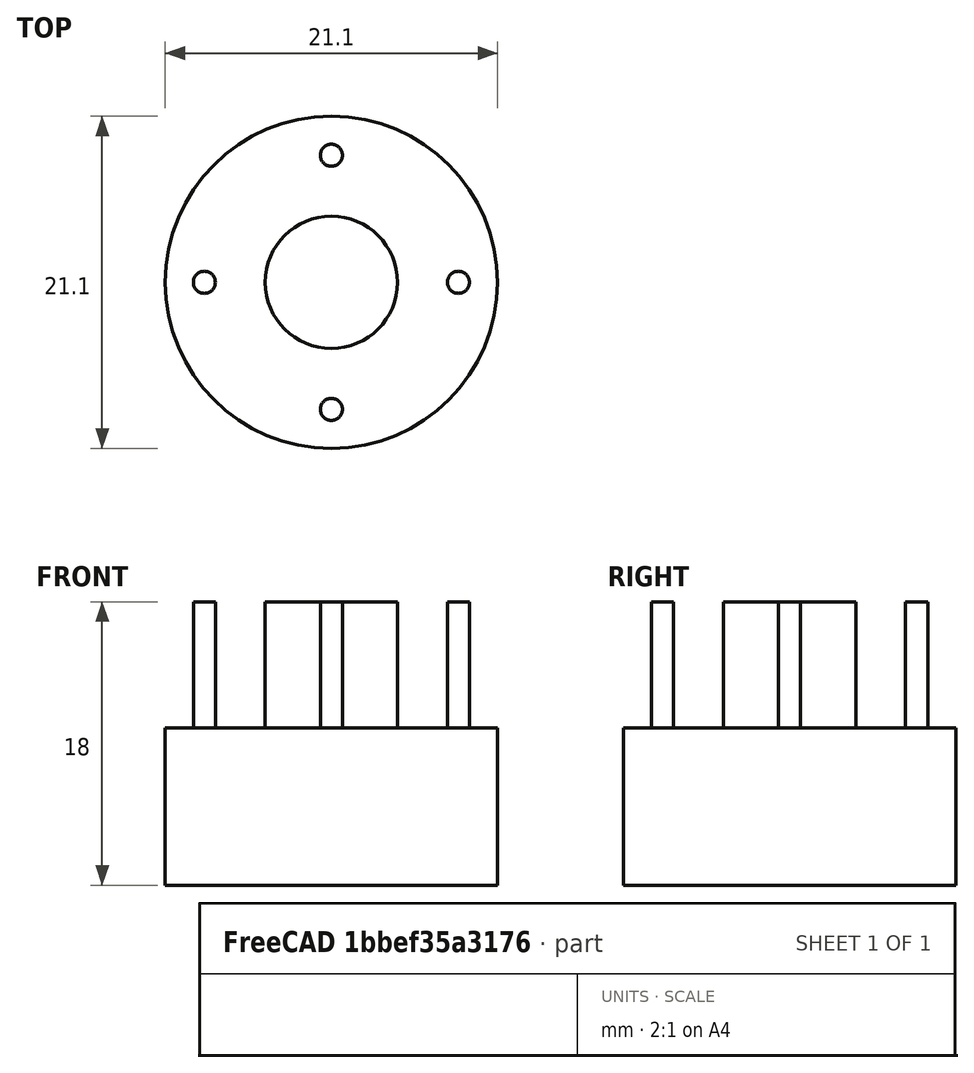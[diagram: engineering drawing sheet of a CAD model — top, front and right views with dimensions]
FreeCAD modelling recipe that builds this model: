
FCSTD DOCUMENT  (FreeCAD 0.16R6706 (Git))
Label: huecohorm
License: All rights reserved
LicenseURL: http://en.wikipedia.org/wiki/All_rights_reserved
objects: Part::Cylinder×3, Part::FeaturePython×1, Part::MultiFuse×1, Part::Feature×1
note: 6 computed .brp shape members not serialized (recipe doc carries the construction recipe); baked Part::Feature solids carry a one-line shape summary decoded from their .brp

FEATURE [Part::Cylinder] Cylinder  label="Cilindro"
  Angle = 360
  Height = 10
  Radius = 10.55
FEATURE [Part::Cylinder] Cylinder001  label="Cilindro001"
  Angle = 360
  Height = 10
  Placement = pos=(0,0,8) rot=(0,0,1;0rad)
  Radius = 4.2
FEATURE [Part::Cylinder] Cylinder002  label="Cilindro002"
  Angle = 360
  Height = 10
  Placement = pos=(0,8.07,8) rot=(0,0,1;0rad)
  Radius = 0.7
FEATURE [Part::FeaturePython] Array  # Draft array (typed FeaturePython)
  Angle = 360
  ArrayType = 1
  Axis = (0,0,1)
  Base = -> Cylinder002
  Center = (0,0,0)
  Fuse = false
  IntervalAxis = (0,0,0)
  IntervalX = (1,0,0)
  IntervalY = (0,1,0)
  IntervalZ = (0,0,0)
  NumberPolar = 4
  NumberX = 2
  NumberY = 2
  NumberZ = 1
FEATURE [Part::MultiFuse] Fusion
  Shapes = -> [Cylinder,Array,Cylinder001]
FEATURE [Part::Feature] Fusion001  label="cdHuecoHorm"
  shape: bbox 21.1 x 21.1 x 18 mm, 13 faces (baked)
